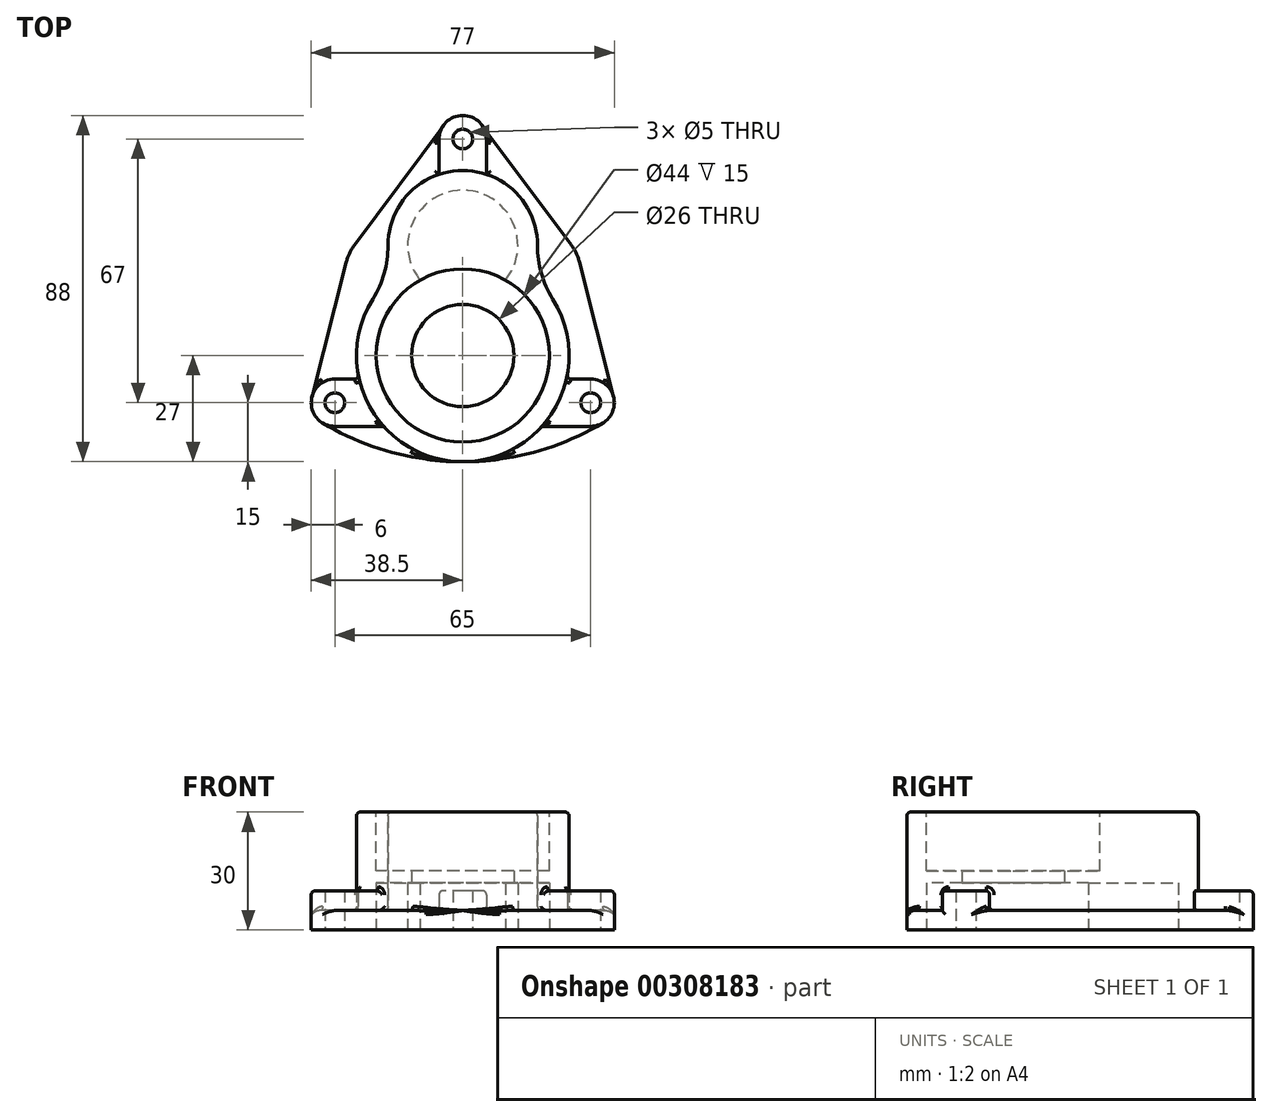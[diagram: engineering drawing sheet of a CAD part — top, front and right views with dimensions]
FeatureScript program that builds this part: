
annotation { "Feature Type Name" : "Feature", "Feature Type Description" : "" }
export const myFeature = defineFeature(function(context is Context, id is Id, definition is map)
    precondition{}
    {
        {
            var Q0;
            Q0=qCreatedBy(makeId("Top.planeOp"),FACE);
            var sketch = newSketch(context, id + "F0", { "sketchPlane" : qUnion([Q0])});
            skCircle(sketch, "E0", {"center": v(0, 0) * mm, "radius": 13 * mm});
            skCircle(sketch, "E1", {"center": v(0, 0) * mm, "radius": 22 * mm});
            skCircle(sketch, "E2", {"center": v(0, 0) * mm, "radius": 27 * mm});
            skCircle(sketch, "E3", {"center": v(32.5, -12) * mm, "radius": 6 * mm});
            skCircle(sketch, "E4", {"center": v(-32.5, -12) * mm, "radius": 6 * mm});
            skCircle(sketch, "E5", {"center": v(-32.5, -12) * mm, "radius": 2.5 * mm});
            skCircle(sketch, "E6", {"center": v(32.5, -12) * mm, "radius": 2.5 * mm});
            skCircle(sketch, "E7", {"center": v(0, 28) * mm, "radius": 14 * mm});
            skArc(sketch, "E8", {"start": v(17.49, 20.57) * mm, "mid": v(0, 47) * mm, "end": v(-17.49, 20.57) * mm});
            skCircle(sketch, "E9", {"center": v(0, 55) * mm, "radius": 6 * mm});
            skCircle(sketch, "E10", {"center": v(0, 55) * mm, "radius": 2.5 * mm});
            skLineSegment(sketch, "E11", {"start": v(-32.5, -18) * mm, "end": v(-20.12, -18) * mm});
            skLineSegment(sketch, "E12", {"start": v(32.5, -18) * mm, "end": v(20.12, -18) * mm});
            skLineSegment(sketch, "E13", {"start": v(32.5, -6) * mm, "end": v(26.32, -6) * mm});
            skLineSegment(sketch, "E14", {"start": v(-32.5, -6) * mm, "end": v(-26.32, -6) * mm});
            skPoint(sketch, "E15.endSnap0", {"position": v(0, 47) * mm});
            skLineSegment(sketch, "E16", {"start": v(6, 55) * mm, "end": v(6, 46.03) * mm});
            skLineSegment(sketch, "E17", {"start": v(-6, 55) * mm, "end": v(-6, 46.03) * mm});
            skArc(sketch, "E18", {"start": v(-27.52, 28.03) * mm, "mid": v(-28.77, 25.95) * mm, "end": v(-29.6, 23.66) * mm});
            skArc(sketch, "E19.trimOffspring", {"start": v(29.61, 23.79) * mm, "mid": v(28.78, 26.1) * mm, "end": v(27.51, 28.2) * mm});
            skLineSegment(sketch, "E20", {"start": v(-4.82, 58.58) * mm, "end": v(-27.52, 28.03) * mm});
            skLineSegment(sketch, "E21", {"start": v(4.8, 58.6) * mm, "end": v(27.51, 28.2) * mm});
            skLineSegment(sketch, "E22", {"start": v(-29.6, 23.66) * mm, "end": v(-38.31, -10.52) * mm});
            skLineSegment(sketch, "E23", {"start": v(29.61, 23.79) * mm, "end": v(38.32, -10.52) * mm});
            skArc(sketch, "E24", {"start": v(0, -27) * mm, "mid": v(18.46, -24.5) * mm, "end": v(35.59, -17.15) * mm});
            skArc(sketch, "E25", {"start": v(-35.59, -17.15) * mm, "mid": v(-18.46, -24.5) * mm, "end": v(0, -27) * mm});
            skPoint(sketch, "E26.orphan", {"position": v(35.59, -17.15) * mm});
            skSolve(sketch);
        }
        {
            var Q0;
            {var subQ0=sQuery(id+"F0.wireOp",EDGE,"E8");var subQ1=sQuery(id+"F0.wireOp",EDGE,"E2");var subQ2=makeQuery(id+"F0.imprint","INTERSECT",VERTEX,{"disambiguationData":[OD(0.0)],"derivedFrom":[subQ1,subQ0]});Q0=makeQuery(id+"F0.imprint","IMPRINT",FACE,{"disambiguationData":[TD([[makeQuery(id+"F0.imprint","IMPRINT",EDGE,{"disambiguationData":[TD([[subQ2,-1.0]])],"derivedFrom":subQ1}),-1.0]])]});}
            var Q1;
            {var subQ0=sQuery(id+"F0.wireOp",EDGE,"E7");var subQ1=sQuery(id+"F0.wireOp",EDGE,"E1");var subQ2=makeQuery(id+"F0.imprint","INTERSECT",VERTEX,{"disambiguationData":[OD(0.0)],"derivedFrom":[subQ1,subQ0]});Q1=makeQuery(id+"F0.imprint","IMPRINT",FACE,{"disambiguationData":[TD([[makeQuery(id+"F0.imprint","IMPRINT",EDGE,{"disambiguationData":[TD([[subQ2,-1.0]])],"derivedFrom":subQ1}),-1.0]])]});}
            var Q2;
            {var subQ0=sQuery(id+"F0.wireOp",EDGE,"E7");var subQ1=sQuery(id+"F0.wireOp",EDGE,"E1");var subQ2=makeQuery(id+"F0.imprint","INTERSECT",VERTEX,{"disambiguationData":[OD(0.0)],"derivedFrom":[subQ1,subQ0]});Q2=makeQuery(id+"F0.imprint","IMPRINT",FACE,{"disambiguationData":[TD([[makeQuery(id+"F0.imprint","IMPRINT",EDGE,{"disambiguationData":[TD([[subQ2,1.0]])],"derivedFrom":subQ1}),-1.0]])]});}
            var Q3;
            {var subQ0=sQuery(id+"F0.wireOp",EDGE,"E7");var subQ1=sQuery(id+"F0.wireOp",EDGE,"E1");var subQ2=makeQuery(id+"F0.imprint","INTERSECT",VERTEX,{"disambiguationData":[OD(0.0)],"derivedFrom":[subQ1,subQ0]});Q3=makeQuery(id+"F0.imprint","IMPRINT",FACE,{"disambiguationData":[TD([[makeQuery(id+"F0.imprint","IMPRINT",EDGE,{"disambiguationData":[TD([[subQ2,1.0]])],"derivedFrom":subQ1}),1.0]])]});}
            var Q4;
            Q4=makeQuery(id+"F0.imprint","IMPRINT",FACE,{"disambiguationData":[TD([[makeQuery(id+"F0.imprint","IMPRINT",EDGE,{"derivedFrom":sQuery(id+"F0.wireOp",EDGE,"E0")}),-1.0]])]});
            var Q5;
            {var subQ0=sQuery(id+"F0.wireOp",EDGE,"E7");var subQ1=sQuery(id+"F0.wireOp",EDGE,"E2");var subQ2=makeQuery(id+"F0.imprint","INTERSECT",VERTEX,{"disambiguationData":[OD(0.0)],"derivedFrom":[subQ1,subQ0]});Q5=makeQuery(id+"F0.imprint","IMPRINT",FACE,{"disambiguationData":[TD([[makeQuery(id+"F0.imprint","IMPRINT",EDGE,{"disambiguationData":[TD([[subQ2,-1.0]])],"derivedFrom":subQ1}),-1.0]])]});}
            var Q6;
            Q6=makeQuery(id+"F0.imprint","IMPRINT",FACE,{"disambiguationData":[TD([[makeQuery(id+"F0.imprint","IMPRINT",EDGE,{"derivedFrom":sQuery(id+"F0.wireOp",EDGE,"E0")}),1.0]])]});
            extrude(context, id + "F1", {"entities" : qUnion([Q0, Q1, Q2, Q3, Q4, Q5, Q6]), "depth" : 30 * mm});
        }
        {
            var Q0;
            {var subQ0=sQuery(id+"F0.wireOp",EDGE,"E8");var subQ1=sQuery(id+"F0.wireOp",EDGE,"E2");Q0=makeQuery(id+"F1.opExtrude","SWEPT_EDGE",EDGE,{"disambiguationData":[OSD([subQ1,subQ0]),TDD([makeQuery(id+"F0.imprint","INTERSECT",VERTEX,{"disambiguationData":[OD(1.0)],"derivedFrom":[subQ1,subQ0]})])]});}
            var Q1;
            {var subQ0=sQuery(id+"F0.wireOp",EDGE,"E8");var subQ1=sQuery(id+"F0.wireOp",EDGE,"E2");Q1=makeQuery(id+"F1.opExtrude","SWEPT_EDGE",EDGE,{"disambiguationData":[OSD([subQ1,subQ0]),TDD([makeQuery(id+"F0.imprint","INTERSECT",VERTEX,{"disambiguationData":[OD(0.0)],"derivedFrom":[subQ1,subQ0]})])]});}
            fillet(context, id + "F2", {"entities" : qUnion([Q0, Q1]), "radius" : 25 * mm, "tangentPropagation" : true, "allowEdgeOverflow" : false});
        }
        {
            var Q0;
            {var subQ0=sQuery(id+"F0.wireOp",EDGE,"E16");Q0=makeQuery(id+"F0.imprint","IMPRINT",FACE,{"disambiguationData":[TD([[makeQuery(id+"F0.imprint","IMPRINT",EDGE,{"derivedFrom":subQ0}),-1.0]])]});}
            var Q1;
            {var subQ0=sQuery(id+"F0.wireOp",EDGE,"E12");Q1=makeQuery(id+"F0.imprint","IMPRINT",FACE,{"disambiguationData":[TD([[makeQuery(id+"F0.imprint","IMPRINT",EDGE,{"derivedFrom":subQ0}),-1.0]])]});}
            var Q2;
            Q2=makeQuery(id+"F0.imprint","IMPRINT",FACE,{"disambiguationData":[TD([[makeQuery(id+"F0.imprint","IMPRINT",EDGE,{"derivedFrom":sQuery(id+"F0.wireOp",EDGE,"E6")}),-1.0]])]});
            var Q3;
            {var subQ0=sQuery(id+"F0.wireOp",EDGE,"E11");Q3=makeQuery(id+"F0.imprint","IMPRINT",FACE,{"disambiguationData":[TD([[makeQuery(id+"F0.imprint","IMPRINT",EDGE,{"derivedFrom":subQ0}),1.0]])]});}
            var Q4;
            Q4=makeQuery(id+"F0.imprint","IMPRINT",FACE,{"disambiguationData":[TD([[makeQuery(id+"F0.imprint","IMPRINT",EDGE,{"derivedFrom":sQuery(id+"F0.wireOp",EDGE,"E5")}),-1.0]])]});
            var Q5;
            Q5=makeQuery(id+"F0.imprint","IMPRINT",FACE,{"disambiguationData":[TD([[makeQuery(id+"F0.imprint","IMPRINT",EDGE,{"derivedFrom":sQuery(id+"F0.wireOp",EDGE,"E10")}),-1.0]])]});
            extrude(context, id + "F3", {"entities" : qUnion([Q0, Q1, Q2, Q3, Q4, Q5]), "operationType" : NewBodyOperationType.ADD, "depth" : 10 * mm});
        }
        {
            var Q0;
            {var subQ4=sQuery(id+"F0.wireOp",EDGE,"E14");Q0=makeQuery(id+"F0.imprint","IMPRINT",FACE,{"disambiguationData":[TD([[makeQuery(id+"F0.imprint","IMPRINT",EDGE,{"derivedFrom":subQ4}),1.0]])]});}
            var Q1;
            {var subQ3=sQuery(id+"F0.wireOp",EDGE,"E13");Q1=makeQuery(id+"F0.imprint","IMPRINT",FACE,{"disambiguationData":[TD([[makeQuery(id+"F0.imprint","IMPRINT",EDGE,{"derivedFrom":subQ3}),-1.0]])]});}
            var Q2;
            {var subQ0=sQuery(id+"F0.wireOp",EDGE,"E12");Q2=makeQuery(id+"F0.imprint","IMPRINT",FACE,{"disambiguationData":[TD([[makeQuery(id+"F0.imprint","IMPRINT",EDGE,{"derivedFrom":subQ0}),1.0]])]});}
            var Q3;
            {var subQ0=sQuery(id+"F0.wireOp",EDGE,"E11");Q3=makeQuery(id+"F0.imprint","IMPRINT",FACE,{"disambiguationData":[TD([[makeQuery(id+"F0.imprint","IMPRINT",EDGE,{"derivedFrom":subQ0}),-1.0]])]});}
            extrude(context, id + "F4", {"entities" : qUnion([Q0, Q1, Q2, Q3]), "operationType" : NewBodyOperationType.ADD, "depth" : 5 * mm});
        }
        {
            var Q0;
            {var subQ0=sQuery(id+"F0.wireOp",EDGE,"E7");var subQ1=sQuery(id+"F0.wireOp",EDGE,"E2");var subQ2=makeQuery(id+"F0.imprint","INTERSECT",VERTEX,{"disambiguationData":[OD(0.0)],"derivedFrom":[subQ1,subQ0]});Q0=makeQuery(id+"F0.imprint","IMPRINT",FACE,{"disambiguationData":[TD([[makeQuery(id+"F0.imprint","IMPRINT",EDGE,{"disambiguationData":[TD([[subQ2,-1.0]])],"derivedFrom":subQ1}),-1.0]])]});}
            var Q1;
            {var subQ0=sQuery(id+"F0.wireOp",EDGE,"E7");var subQ1=sQuery(id+"F0.wireOp",EDGE,"E1");var subQ2=makeQuery(id+"F0.imprint","INTERSECT",VERTEX,{"disambiguationData":[OD(0.0)],"derivedFrom":[subQ1,subQ0]});Q1=makeQuery(id+"F0.imprint","IMPRINT",FACE,{"disambiguationData":[TD([[makeQuery(id+"F0.imprint","IMPRINT",EDGE,{"disambiguationData":[TD([[subQ2,1.0]])],"derivedFrom":subQ1}),-1.0]])]});}
            var Q2;
            {var subQ0=sQuery(id+"F0.wireOp",EDGE,"E7");var subQ1=sQuery(id+"F0.wireOp",EDGE,"E1");var subQ2=makeQuery(id+"F0.imprint","INTERSECT",VERTEX,{"disambiguationData":[OD(0.0)],"derivedFrom":[subQ1,subQ0]});Q2=makeQuery(id+"F0.imprint","IMPRINT",FACE,{"disambiguationData":[TD([[makeQuery(id+"F0.imprint","IMPRINT",EDGE,{"disambiguationData":[TD([[subQ2,1.0]])],"derivedFrom":subQ1}),1.0]])]});}
            var Q3;
            Q3=makeQuery(id+"F0.imprint","IMPRINT",FACE,{"disambiguationData":[TD([[makeQuery(id+"F0.imprint","IMPRINT",EDGE,{"derivedFrom":sQuery(id+"F0.wireOp",EDGE,"E0")}),-1.0]])]});
            var Q4;
            Q4=makeQuery(id+"F0.imprint","IMPRINT",FACE,{"disambiguationData":[TD([[makeQuery(id+"F0.imprint","IMPRINT",EDGE,{"derivedFrom":sQuery(id+"F0.wireOp",EDGE,"E0")}),1.0]])]});
            extrude(context, id + "F5", {"entities" : qUnion([Q0, Q1, Q2, Q3, Q4]), "operationType" : NewBodyOperationType.REMOVE, "depth" : 12 * mm});
        }
        {
            var Q0;
            Q0=makeQuery(id+"F1.opExtrude","CAP_FACE",FACE,{"disambiguationData":[OSD([sQuery(id+"F0.wireOp",EDGE,"E2"),sQuery(id+"F0.wireOp",EDGE,"E8")])],"isStart":false});
            var sketch = newSketch(context, id + "F6", { "sketchPlane" : qUnion([Q0])});
            skCircle(sketch, "E27.0", {"center": v(0, 0) * mm, "radius": 22 * mm});
            skSolve(sketch);
        }
        {
            var Q0;
            Q0=qSketchRegion(id+"F6",true);
            extrude(context, id + "F7", {"entities" : qUnion([Q0]), "operationType" : NewBodyOperationType.REMOVE, "oppositeDirection" : true, "depth" : 15 * mm});
        }
        {
            var Q0;
            Q0=makeQuery(id+"F0.imprint","IMPRINT",FACE,{"disambiguationData":[TD([[makeQuery(id+"F0.imprint","IMPRINT",EDGE,{"derivedFrom":sQuery(id+"F0.wireOp",EDGE,"E0")}),1.0]])]});
            extrude(context, id + "F8", {"entities" : qUnion([Q0]), "operationType" : NewBodyOperationType.REMOVE, "endBound" : BoundingType.THROUGH_ALL, "depth" : 25 * mm});
        }
        {
            var Q0;
            Q0=makeQuery(id+"F4.opExtrude","CAP_FACE",FACE,{"disambiguationData":[OSD([sQuery(id+"F0.wireOp",EDGE,"E2"),sQuery(id+"F0.wireOp",EDGE,"E3"),sQuery(id+"F0.wireOp",EDGE,"E8"),sQuery(id+"F0.wireOp",EDGE,"E9"),sQuery(id+"F0.wireOp",EDGE,"E13"),sQuery(id+"F0.wireOp",EDGE,"E16"),sQuery(id+"F0.wireOp",EDGE,"E19.trimOffspring"),sQuery(id+"F0.wireOp",EDGE,"E21"),sQuery(id+"F0.wireOp",EDGE,"E23")])],"isStart":false});
            var Q1;
            Q1=makeQuery(id+"F4.opExtrude","CAP_FACE",FACE,{"disambiguationData":[OSD([sQuery(id+"F0.wireOp",EDGE,"E2"),sQuery(id+"F0.wireOp",EDGE,"E4"),sQuery(id+"F0.wireOp",EDGE,"E8"),sQuery(id+"F0.wireOp",EDGE,"E9"),sQuery(id+"F0.wireOp",EDGE,"E14"),sQuery(id+"F0.wireOp",EDGE,"E17"),sQuery(id+"F0.wireOp",EDGE,"E18"),sQuery(id+"F0.wireOp",EDGE,"E20"),sQuery(id+"F0.wireOp",EDGE,"E22")])],"isStart":false});
            var Q2;
            Q2=makeQuery(id+"F3.opExtrude","CAP_EDGE",EDGE,{"disambiguationData":[OSD([sQuery(id+"F0.wireOp",EDGE,"E16")])],"isStart":false});
            var Q3;
            Q3=makeQuery(id+"F3.opExtrude","CAP_EDGE",EDGE,{"disambiguationData":[OSD([sQuery(id+"F0.wireOp",EDGE,"E12")])],"isStart":false});
            var Q4;
            Q4=makeQuery(id+"F3.opExtrude","CAP_EDGE",EDGE,{"disambiguationData":[OSD([sQuery(id+"F0.wireOp",EDGE,"E11")])],"isStart":false});
            var Q5;
            Q5=makeQuery(id+"F4.opExtrude","CAP_EDGE",EDGE,{"disambiguationData":[OSD([sQuery(id+"F0.wireOp",EDGE,"E12")])],"isStart":false});
            var Q6;
            Q6=makeQuery(id+"F4.opExtrude","CAP_EDGE",EDGE,{"disambiguationData":[OSD([sQuery(id+"F0.wireOp",EDGE,"E11")])],"isStart":false});
            var Q7;
            {var subQ0=sQuery(id+"F0.wireOp",EDGE,"E2");Q7=makeQuery(id+"F4.opExtrude","CAP_EDGE",EDGE,{"disambiguationData":[OSD([subQ0]),TDD([makeQuery(id+"F0.imprint","IMPRINT",EDGE,{"disambiguationData":[TD([[makeQuery(id+"F0.imprint","INTERSECT",VERTEX,{"derivedFrom":[subQ0,sQuery(id+"F0.wireOp",EDGE,"E11")]}),-1.0]])],"derivedFrom":subQ0})])],"isStart":false});}
            var Q8;
            {var subQ0=sQuery(id+"F0.wireOp",EDGE,"E2");Q8=makeQuery(id+"F4.opExtrude","CAP_EDGE",EDGE,{"disambiguationData":[OSD([subQ0]),TDD([makeQuery(id+"F0.imprint","IMPRINT",EDGE,{"disambiguationData":[TD([[makeQuery(id+"F0.imprint","INTERSECT",VERTEX,{"derivedFrom":[subQ0,sQuery(id+"F0.wireOp",EDGE,"E12")]}),1.0]])],"derivedFrom":subQ0})])],"isStart":false});}
            fillet(context, id + "F9", {"entities" : qUnion([Q0, Q1, Q2, Q3, Q4, Q5, Q6, Q7, Q8]), "radius" : 1 * mm, "tangentPropagation" : true, "allowEdgeOverflow" : false});
        }
        {
            var Q0;
            Q0=makeQuery(id+"F4.opExtrude","CAP_EDGE",EDGE,{"disambiguationData":[OSD([sQuery(id+"F0.wireOp",EDGE,"E25")])],"isStart":false});
            var Q1;
            Q1=makeQuery(id+"F4.opExtrude","CAP_EDGE",EDGE,{"disambiguationData":[OSD([sQuery(id+"F0.wireOp",EDGE,"E24")])],"isStart":false});
            fillet(context, id + "F10", {"entities" : qUnion([Q0, Q1]), "radius" : 1 * mm, "tangentPropagation" : true, "allowEdgeOverflow" : false});
        }
        {
            var Q0;
            Q0=makeQuery(id+"F1.opExtrude","SWEPT_FACE",FACE,{"disambiguationData":[OSD([sQuery(id+"F0.wireOp",EDGE,"E2")])]});
            fillet(context, id + "F11", {"entities" : qUnion([Q0]), "radius" : 1 * mm, "tangentPropagation" : true, "allowEdgeOverflow" : false});
        }
    });
